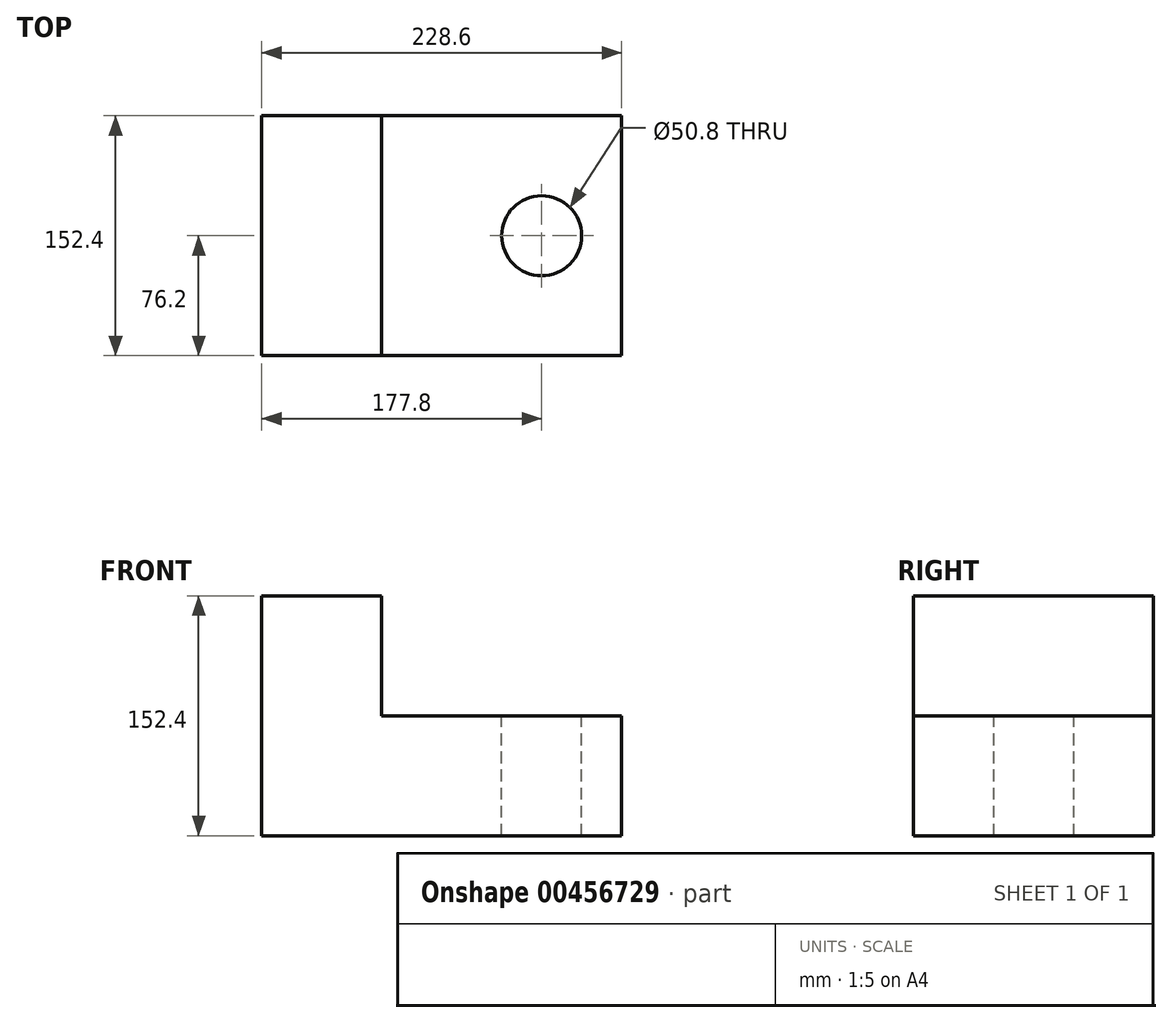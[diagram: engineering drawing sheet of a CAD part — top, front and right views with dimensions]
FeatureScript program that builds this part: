
annotation { "Feature Type Name" : "Feature", "Feature Type Description" : "" }
export const myFeature = defineFeature(function(context is Context, id is Id, definition is map)
    precondition{}
    {
        {
            var Q0;
            Q0=qCreatedBy(makeId("Front.planeOp"),FACE);
            var sketch = newSketch(context, id + "F0", { "sketchPlane" : qUnion([Q0])});
            skLineSegment(sketch, "E0", {"start": v(0, 0) * mm, "end": v(-228.6, 0) * mm});
            skLineSegment(sketch, "E1", {"start": v(-228.6, 0) * mm, "end": v(-228.6, 152.4) * mm});
            skLineSegment(sketch, "E2", {"start": v(-228.6, 152.4) * mm, "end": v(-152.4, 152.4) * mm});
            skLineSegment(sketch, "E3", {"start": v(-152.4, 152.4) * mm, "end": v(-152.4, 76.2) * mm});
            skLineSegment(sketch, "E4", {"start": v(-152.4, 76.2) * mm, "end": v(0, 76.2) * mm});
            skLineSegment(sketch, "E5", {"start": v(0, 76.2) * mm, "end": v(0, 0) * mm});
            skSolve(sketch);
        }
        {
            var Q0;
            Q0=makeQuery(id+"F0.imprint","IMPRINT",FACE,{"disambiguationData":[TD([[makeQuery(id+"F0.imprint","IMPRINT",EDGE,{"derivedFrom":sQuery(id+"F0.wireOp",EDGE,"E0")}),-1.0]])]});
            extrude(context, id + "F1", {"entities" : qUnion([Q0]), "depth" : 152.4 * mm});
        }
        {
            var Q0;
            Q0=makeQuery(id+"F1.opExtrude","SWEPT_FACE",FACE,{"disambiguationData":[OSD([sQuery(id+"F0.wireOp",EDGE,"E4")])]});
            var sketch = newSketch(context, id + "F2", { "sketchPlane" : qUnion([Q0])});
            skPoint(sketch, "E6", {"position": v(-50.8, -76.2) * mm});
            skSolve(sketch);
        }
        {
            var Q0;
            Q0=sQuery(id+"F2.wireOp",VERTEX,"E6");
            var Q1;
            Q1=makeQuery(id+"F1.opExtrude","SWEPT_BODY",BODY,{"disambiguationData":[OSD([sQuery(id+"F0.wireOp",EDGE,"E0"),sQuery(id+"F0.wireOp",EDGE,"E1"),sQuery(id+"F0.wireOp",EDGE,"E2"),sQuery(id+"F0.wireOp",EDGE,"E3"),sQuery(id+"F0.wireOp",EDGE,"E4"),sQuery(id+"F0.wireOp",EDGE,"E5")])]});
            hole(context, id + "F3", {"style" : HoleStyle.SIMPLE, "endStyle" : HoleEndStyle.THROUGH, "holeDiameter" : 50.8 * mm, "isTappedThrough" : true, "tappedDepth" : 12.7 * mm, "tapClearance" : 3, "locations" : qUnion([Q0]), "scope" : qUnion([Q1])});
        }
    });
